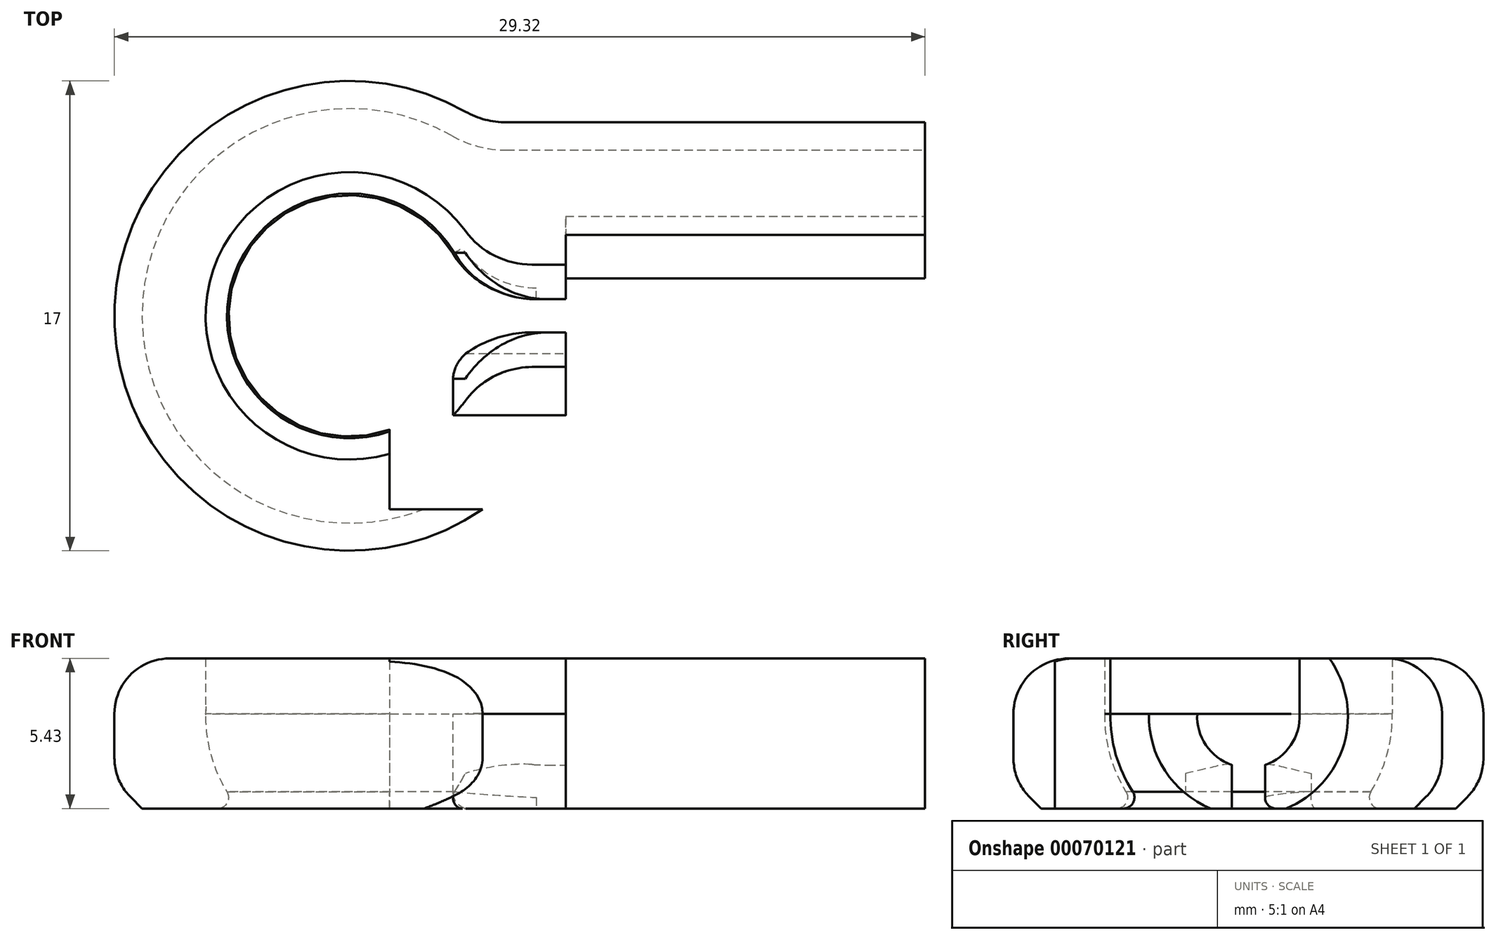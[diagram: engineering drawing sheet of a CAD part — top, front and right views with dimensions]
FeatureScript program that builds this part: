
annotation { "Feature Type Name" : "Feature", "Feature Type Description" : "" }
export const myFeature = defineFeature(function(context is Context, id is Id, definition is map)
    precondition{}
    {
        {
            assignVariable(context, id + "F0", {"name" : "ball", "anyValue" : 10});
        }
        {
            var Q0;
            Q0=qCreatedBy(makeId("Top.planeOp"),FACE);
            var sketch = newSketch(context, id + "F1", { "sketchPlane" : qUnion([Q0])});
            skCircle(sketch, "E0", {"center": v(0, 0) * mm, "radius": 5.2 * mm});
            skLineSegment(sketch, "E1", {"start": v(-13.72, 0) * mm, "end": v(11.71, 0) * mm});
            skCircle(sketch, "E2.0", {"center": v(0, 0) * mm, "radius": 8.5 * mm});
            skCircle(sketch, "E3", {"center": v(-8.1, 0) * mm, "radius": 2.9 * mm, "construction": true});
            skCircle(sketch, "E4", {"center": v(-8.1, 0) * mm, "radius": 1.4 * mm, "construction": true});
            skLineSegment(sketch, "E5.rect.bottom", {"start": v(4.82, 7) * mm, "end": v(20.82, 7) * mm});
            skLineSegment(sketch, "E5.rect.top", {"start": v(4.82, -7) * mm, "end": v(20.82, -7) * mm});
            skLineSegment(sketch, "E5.rect.left", {"start": v(4.82, 7) * mm, "end": v(4.82, -7) * mm, "construction": true});
            skLineSegment(sketch, "E5.rect.right", {"start": v(20.82, 7) * mm, "end": v(20.82, -7) * mm});
            skPoint(sketch, "E5.rect.middle", {"position": v(12.82, 0) * mm});
            skSolve(sketch);
        }
        {
            var Q0;
            {var subQ0=sQuery(id+"F1.wireOp",EDGE,"E1");var subQ1=sQuery(id+"F1.wireOp",EDGE,"E0");var subQ2=makeQuery(id+"F1.imprint","INTERSECT",VERTEX,{"disambiguationData":[OD(0.0)],"derivedFrom":[subQ1,subQ0]});Q0=makeQuery(id+"F1.imprint","IMPRINT",FACE,{"disambiguationData":[TD([[makeQuery(id+"F1.imprint","IMPRINT",EDGE,{"disambiguationData":[TD([[subQ2,-1.0]])],"derivedFrom":subQ1}),-1.0]])]});}
            var Q1;
            {var subQ0=sQuery(id+"F1.wireOp",EDGE,"E1");var subQ1=sQuery(id+"F1.wireOp",EDGE,"E0");var subQ2=makeQuery(id+"F1.imprint","INTERSECT",VERTEX,{"disambiguationData":[OD(0.0)],"derivedFrom":[subQ1,subQ0]});Q1=makeQuery(id+"F1.imprint","IMPRINT",FACE,{"disambiguationData":[TD([[makeQuery(id+"F1.imprint","IMPRINT",EDGE,{"disambiguationData":[TD([[subQ2,1.0]])],"derivedFrom":subQ1}),-1.0]])]});}
            var Q2;
            {var subQ4=sQuery(id+"F1.wireOp",EDGE,"E5.rect.bottom");Q2=makeQuery(id+"F1.imprint","IMPRINT",FACE,{"disambiguationData":[TD([[makeQuery(id+"F1.imprint","IMPRINT",EDGE,{"derivedFrom":subQ4}),-1.0]])]});}
            var Q3;
            {var subQ0=sQuery(id+"F1.wireOp",EDGE,"E2.0");var subQ1=sQuery(id+"F1.wireOp",EDGE,"E1");var subQ2=makeQuery(id+"F1.imprint","INTERSECT",VERTEX,{"disambiguationData":[OD(0.0)],"derivedFrom":[subQ1,subQ0]});Q3=makeQuery(id+"F1.imprint","IMPRINT",FACE,{"disambiguationData":[TD([[makeQuery(id+"F1.imprint","IMPRINT",EDGE,{"disambiguationData":[TD([[subQ2,1.0]])],"derivedFrom":subQ1}),1.0]])]});}
            var Q4;
            {var subQ0=sQuery(id+"F1.wireOp",EDGE,"E2.0");var subQ1=sQuery(id+"F1.wireOp",EDGE,"E1");var subQ2=makeQuery(id+"F1.imprint","INTERSECT",VERTEX,{"disambiguationData":[OD(0.0)],"derivedFrom":[subQ1,subQ0]});Q4=makeQuery(id+"F1.imprint","IMPRINT",FACE,{"disambiguationData":[TD([[makeQuery(id+"F1.imprint","IMPRINT",EDGE,{"disambiguationData":[TD([[subQ2,1.0]])],"derivedFrom":subQ1}),-1.0]])]});}
            var Q5;
            {var subQ0=sQuery(id+"F1.wireOp",EDGE,"E4");var subQ1=sQuery(id+"F1.wireOp",EDGE,"E1");var subQ2=makeQuery(id+"F1.imprint","INTERSECT",VERTEX,{"disambiguationData":[OD(1.0)],"derivedFrom":[subQ1,subQ0]});Q5=makeQuery(id+"F1.imprint","IMPRINT",FACE,{"disambiguationData":[TD([[makeQuery(id+"F1.imprint","IMPRINT",EDGE,{"disambiguationData":[TD([[subQ2,-1.0]])],"derivedFrom":subQ1}),1.0]])]});}
            var Q6;
            {var subQ0=sQuery(id+"F1.wireOp",EDGE,"E4");var subQ1=sQuery(id+"F1.wireOp",EDGE,"E1");var subQ2=makeQuery(id+"F1.imprint","INTERSECT",VERTEX,{"disambiguationData":[OD(1.0)],"derivedFrom":[subQ1,subQ0]});Q6=makeQuery(id+"F1.imprint","IMPRINT",FACE,{"disambiguationData":[TD([[makeQuery(id+"F1.imprint","IMPRINT",EDGE,{"disambiguationData":[TD([[subQ2,-1.0]])],"derivedFrom":subQ1}),-1.0]])]});}
            var Q7;
            {var subQ0=sQuery(id+"F1.wireOp",EDGE,"E1");var subQ1=sQuery(id+"F1.wireOp",EDGE,"E0");var subQ2=makeQuery(id+"F1.imprint","INTERSECT",VERTEX,{"disambiguationData":[OD(0.0)],"derivedFrom":[subQ1,subQ0]});Q7=makeQuery(id+"F1.imprint","IMPRINT",FACE,{"disambiguationData":[TD([[makeQuery(id+"F1.imprint","IMPRINT",EDGE,{"disambiguationData":[TD([[subQ2,1.0]])],"derivedFrom":subQ1}),1.0]])]});}
            var Q8;
            {var subQ0=sQuery(id+"F1.wireOp",EDGE,"E1");var subQ1=sQuery(id+"F1.wireOp",EDGE,"E0");var subQ2=makeQuery(id+"F1.imprint","INTERSECT",VERTEX,{"disambiguationData":[OD(0.0)],"derivedFrom":[subQ1,subQ0]});Q8=makeQuery(id+"F1.imprint","IMPRINT",FACE,{"disambiguationData":[TD([[makeQuery(id+"F1.imprint","IMPRINT",EDGE,{"disambiguationData":[TD([[subQ2,-1.0]])],"derivedFrom":subQ1}),1.0]])]});}
            extrude(context, id + "F2", {"entities" : qUnion([Q0, Q1, Q2, Q3, Q4, Q5, Q6, Q7, Q8]), "depth" : 0.1 * mm, "hasSecondDirection" : true, "secondDirectionOppositeDirection" : true, "secondDirectionDepth" : (getVariable(context, 'ball') / 3) * mm});
        }
        {
            var Q0;
            {var subQ0=sQuery(id+"F1.wireOp",EDGE,"E1");var subQ1=sQuery(id+"F1.wireOp",EDGE,"E0");var subQ2=makeQuery(id+"F1.imprint","INTERSECT",VERTEX,{"disambiguationData":[OD(0.0)],"derivedFrom":[subQ1,subQ0]});Q0=makeQuery(id+"F1.imprint","IMPRINT",FACE,{"disambiguationData":[TD([[makeQuery(id+"F1.imprint","IMPRINT",EDGE,{"disambiguationData":[TD([[subQ2,-1.0]])],"derivedFrom":subQ1}),1.0]])]});}
            var Q1;
            Q1=sQuery(id+"F1.wireOp",EDGE,"E1");
            revolve(context, id + "F3", {"operationType" : NewBodyOperationType.REMOVE, "entities" : qUnion([Q0]), "axis" : qUnion([Q1]), "revolveType" : RevolveType.FULL, "oppositeDirection" : true});
        }
        {
            var Q0;
            Q0=makeQuery(id+"F2.opExtrude","SWEPT_FACE",FACE,{"disambiguationData":[OSD([sQuery(id+"F1.wireOp",EDGE,"E5.rect.right")])]});
            var sketch = newSketch(context, id + "F4", { "sketchPlane" : qUnion([Q0])});
            skArc(sketch, "E6", {"start": v(-1.85, 3.09) * mm, "mid": v(0, -3.6) * mm, "end": v(1.85, 3.09) * mm});
            skArc(sketch, "E7", {"start": v(-1.85, 0.1) * mm, "mid": v(0, -1.85) * mm, "end": v(1.85, 0.1) * mm});
            skLineSegment(sketch, "E8.bottom", {"start": v(1.85, 0.1) * mm, "end": v(-1.85, 0.1) * mm});
            skLineSegment(sketch, "E8.top", {"start": v(1.85, 5.18) * mm, "end": v(-1.85, 5.18) * mm});
            skLineSegment(sketch, "E8.left", {"start": v(1.85, 0.1) * mm, "end": v(1.85, 5.18) * mm});
            skLineSegment(sketch, "E8.right", {"start": v(-1.85, 0.1) * mm, "end": v(-1.85, 5.18) * mm});
            skPoint(sketch, "E8.middle", {"position": v(0, 2.64) * mm});
            skSolve(sketch);
        }
        {
            var Q0;
            Q0=makeQuery(id+"F2.opExtrude","CAP_FACE",FACE,{"disambiguationData":[OSD([sQuery(id+"F1.wireOp",EDGE,"E2.0"),sQuery(id+"F1.wireOp",EDGE,"E4"),sQuery(id+"F1.wireOp",EDGE,"E5.rect.bottom"),sQuery(id+"F1.wireOp",EDGE,"E5.rect.top"),sQuery(id+"F1.wireOp",EDGE,"E5.rect.right")])],"isStart":false});
            var sketch = newSketch(context, id + "F5", { "sketchPlane" : qUnion([Q0])});
            skPoint(sketch, "E9.0", {"position": v(0, 0) * mm});
            skCircle(sketch, "E10", {"center": v(0, 0) * mm, "radius": 5.8 * mm, "construction": true});
            skCircle(sketch, "E11.0", {"center": v(0, 0) * mm, "radius": 6 * mm, "construction": true});
            skLineSegment(sketch, "E12.rect.bottom", {"start": v(-5.78, 0.5) * mm, "end": v(0.17, 0.5) * mm, "construction": true});
            skLineSegment(sketch, "E12.rect.top", {"start": v(-5.78, -0.5) * mm, "end": v(0.17, -0.5) * mm, "construction": true});
            skLineSegment(sketch, "E12.rect.left", {"start": v(-5.78, 0.5) * mm, "end": v(-5.78, -0.5) * mm, "construction": true});
            skLineSegment(sketch, "E12.rect.right", {"start": v(0.17, 0.5) * mm, "end": v(0.17, -0.5) * mm, "construction": true});
            skPoint(sketch, "E12.rect.middle", {"position": v(-2.8, 0) * mm});
            skLineSegment(sketch, "E13.bottom", {"start": v(19.5, 0.6) * mm, "end": v(-3.53, 0.6) * mm});
            skLineSegment(sketch, "E13.top", {"start": v(19.5, -0.6) * mm, "end": v(-3.53, -0.6) * mm});
            skLineSegment(sketch, "E13.left", {"start": v(19.5, 0.6) * mm, "end": v(19.5, -0.6) * mm});
            skLineSegment(sketch, "E13.right", {"start": v(-3.53, 0.6) * mm, "end": v(-3.53, -0.6) * mm});
            skPoint(sketch, "E13.middle", {"position": v(7.98, 0) * mm});
            skSolve(sketch);
        }
        {
            var Q0;
            Q0=makeQuery(id+"F2.opExtrude","CAP_FACE",FACE,{"disambiguationData":[OSD([sQuery(id+"F1.wireOp",EDGE,"E2.0"),sQuery(id+"F1.wireOp",EDGE,"E5.rect.bottom"),sQuery(id+"F1.wireOp",EDGE,"E5.rect.top"),sQuery(id+"F1.wireOp",EDGE,"E5.rect.right")])],"isStart":false});
            extrude(context, id + "F6", {"entities" : qUnion([Q0]), "operationType" : NewBodyOperationType.ADD, "depth" : 2 * mm});
        }
        {
            var Q0;
            {var subQ0=sQuery(id+"F5.wireOp",EDGE,"E13.left");Q0=makeQuery(id+"F5.imprint","IMPRINT",FACE,{"disambiguationData":[TD([[makeQuery(id+"F5.imprint","IMPRINT",EDGE,{"derivedFrom":subQ0}),-1.0]])]});}
            var Q1;
            {var subQ0=sQuery(id+"F5.wireOp",EDGE,"E13.right");Q1=makeQuery(id+"F5.imprint","IMPRINT",FACE,{"disambiguationData":[TD([[makeQuery(id+"F5.imprint","IMPRINT",EDGE,{"derivedFrom":subQ0}),1.0]])]});}
            extrude(context, id + "F7", {"entities" : qUnion([Q0, Q1]), "operationType" : NewBodyOperationType.REMOVE, "endBound" : BoundingType.SYMMETRIC, "oppositeDirection" : true, "depth" : 25 * mm});
        }
        {
            var Q0;
            Q0=makeQuery(id+"F4.imprint","IMPRINT",FACE,{"disambiguationData":[TD([[makeQuery(id+"F4.imprint","IMPRINT",EDGE,{"derivedFrom":sQuery(id+"F4.wireOp",EDGE,"E6")}),1.0]])]});
            var Q1;
            {var subQ0=sQuery(id+"F4.wireOp",EDGE,"E6");var subQ1=makeQuery(id+"F2.opExtrude","CAP_EDGE",EDGE,{"disambiguationData":[OSD([sQuery(id+"F1.wireOp",EDGE,"E5.rect.right")])],"isStart":false});var subQ2=makeQuery(id+"F4.imprint","INTERSECT",VERTEX,{"disambiguationData":[OD(0.0)],"derivedFrom":[subQ1,subQ0]});Q1=makeQuery(id+"F4.imprint","IMPRINT",FACE,{"disambiguationData":[TD([[makeQuery(id+"F4.imprint","IMPRINT",EDGE,{"disambiguationData":[TD([[subQ2,1.0]])],"derivedFrom":subQ0}),1.0]])]});}
            var Q2;
            {var subQ0=sQuery(id+"F4.wireOp",EDGE,"E8.left");var subQ1=sQuery(id+"F4.wireOp",EDGE,"E6");var subQ2=makeQuery(id+"F4.imprint","INTERSECT",VERTEX,{"derivedFrom":[subQ1,subQ0]});Q2=makeQuery(id+"F4.imprint","IMPRINT",FACE,{"disambiguationData":[TD([[makeQuery(id+"F4.imprint","IMPRINT",EDGE,{"disambiguationData":[TD([[subQ2,1.0]])],"derivedFrom":subQ1}),1.0]])]});}
            extrude(context, id + "F8", {"entities" : qUnion([Q0, Q1, Q2]), "operationType" : NewBodyOperationType.REMOVE, "oppositeDirection" : true, "depth" : 13 * mm});
        }
        {
            var Q0;
            {var subQ0=sQuery(id+"F1.wireOp",EDGE,"E5.rect.right");Q0=makeQuery(id+"F8.boolean.opBoolean","SPLIT",FACE,{"disambiguationData":[TD([makeQuery(id+"F8.opExtrude","SWEPT_FACE",FACE,{"disambiguationData":[OSD([sQuery(id+"F4.wireOp",EDGE,"E7")])]})])],"derivedFrom":makeQuery(id+"F2.opExtrude","SWEPT_FACE",FACE,{"disambiguationData":[OSD([subQ0])]})});}
            extrude(context, id + "F9", {"entities" : qUnion([Q0]), "operationType" : NewBodyOperationType.REMOVE, "oppositeDirection" : true, "depth" : 19.37 * mm});
        }
        {
            var Q0;
            Q0=makeQuery(id+"F2.opExtrude","SWEPT_EDGE",EDGE,{"disambiguationData":[OSD([sQuery(id+"F1.wireOp",EDGE,"E2.0"),sQuery(id+"F1.wireOp",EDGE,"E5.rect.top")])]});
            var Q1;
            Q1=makeQuery(id+"F2.opExtrude","SWEPT_EDGE",EDGE,{"disambiguationData":[OSD([sQuery(id+"F1.wireOp",EDGE,"E2.0"),sQuery(id+"F1.wireOp",EDGE,"E5.rect.bottom")])]});
            fillet(context, id + "F10", {"entities" : qUnion([Q0, Q1]), "radius" : 3 * mm, "tangentPropagation" : true, "allowEdgeOverflow" : false});
        }
        {
            var Q0;
            Q0=makeQuery(id+"F2.opExtrude","CAP_EDGE",EDGE,{"disambiguationData":[OSD([sQuery(id+"F1.wireOp",EDGE,"E2.0")])],"isStart":true});
            chamfer(context, id + "F11", {"entities" : qUnion([Q0]), "width" : 1 * mm, "tangentPropagation" : true});
        }
        {
            var Q0;
            {var subQ0=sQuery(id+"F1.wireOp",EDGE,"E2.0");Q0=makeQuery(id+"F11.opChamfer","BLEND_EDGE",EDGE,{"blendedFrom":[makeQuery(id+"F2.opExtrude","CAP_EDGE",EDGE,{"disambiguationData":[OSD([subQ0])],"isStart":false}),makeQuery(id+"F2.opExtrude","SWEPT_FACE",FACE,{"disambiguationData":[OSD([subQ0])]})],"blendedInto":[makeQuery(id+"F2.opExtrude","SWEPT_FACE",FACE,{"disambiguationData":[OSD([subQ0])]})]});}
            var Q1;
            {var subQ0=sQuery(id+"F1.wireOp",EDGE,"E2.0");Q1=makeQuery(id+"F11.opChamfer","BLEND_EDGE",EDGE,{"blendedFrom":[makeQuery(id+"F2.opExtrude","CAP_EDGE",EDGE,{"disambiguationData":[OSD([subQ0])],"isStart":true}),makeQuery(id+"F2.opExtrude","SWEPT_FACE",FACE,{"disambiguationData":[OSD([subQ0])]})],"blendedInto":[makeQuery(id+"F2.opExtrude","SWEPT_FACE",FACE,{"disambiguationData":[OSD([subQ0])]})]});}
            var Q2;
            Q2=makeQuery(id+"F6.opExtrude","CAP_EDGE",EDGE,{"disambiguationData":[OSD([sQuery(id+"F1.wireOp",EDGE,"E2.0")])],"isStart":false});
            fillet(context, id + "F12", {"entities" : qUnion([Q0, Q1, Q2]), "radius" : 2 * mm, "tangentPropagation" : true, "allowEdgeOverflow" : false});
        }
        {
            var Q0;
            Q0=makeQuery(id+"F9.boolean.opBoolean","INTERSECT",EDGE,{"derivedFrom":[makeQuery(id+"F3.boolean.opBoolean","COPY",FACE,{"derivedFrom":makeQuery(id+"F3.opRevolve","SWEPT_FACE",FACE,{"disambiguationData":[OSD([sQuery(id+"F1.wireOp",EDGE,"E0")])]})}),makeQuery(id+"F9.opExtrude","SWEPT_FACE",FACE,{"disambiguationData":[OSD([sQuery(id+"F4.wireOp",EDGE,"E7")])]})]});
            var Q1;
            Q1=makeQuery(id+"F9.boolean.opBoolean","INTERSECT",EDGE,{"derivedFrom":[makeQuery(id+"F6.opExtrude","SWEPT_FACE",FACE,{"disambiguationData":[OSD([sQuery(id+"F1.wireOp",EDGE,"E0"),sQuery(id+"F1.wireOp",EDGE,"E2.0"),sQuery(id+"F1.wireOp",EDGE,"E5.rect.bottom"),sQuery(id+"F1.wireOp",EDGE,"E5.rect.top"),sQuery(id+"F1.wireOp",EDGE,"E5.rect.right")])]}),makeQuery(id+"F9.opExtrude","SWEPT_FACE",FACE,{"disambiguationData":[OSD([sQuery(id+"F4.wireOp",EDGE,"E8.right")])]})]});
            var Q2;
            Q2=makeQuery(id+"F9.boolean.opBoolean","INTERSECT",EDGE,{"derivedFrom":[makeQuery(id+"F6.opExtrude","SWEPT_FACE",FACE,{"disambiguationData":[OSD([sQuery(id+"F1.wireOp",EDGE,"E0"),sQuery(id+"F1.wireOp",EDGE,"E2.0"),sQuery(id+"F1.wireOp",EDGE,"E5.rect.bottom"),sQuery(id+"F1.wireOp",EDGE,"E5.rect.top"),sQuery(id+"F1.wireOp",EDGE,"E5.rect.right")])]}),makeQuery(id+"F9.opExtrude","SWEPT_FACE",FACE,{"disambiguationData":[OSD([sQuery(id+"F4.wireOp",EDGE,"E8.left")])]})]});
            var Q3;
            Q3=makeQuery(id+"F7.boolean.opBoolean","INTERSECT",EDGE,{"derivedFrom":[makeQuery(id+"F3.boolean.opBoolean","COPY",FACE,{"derivedFrom":makeQuery(id+"F3.opRevolve","SWEPT_FACE",FACE,{"disambiguationData":[OSD([sQuery(id+"F1.wireOp",EDGE,"E0")])]})}),makeQuery(id+"F7.opExtrude","SWEPT_FACE",FACE,{"disambiguationData":[OSD([sQuery(id+"F5.wireOp",EDGE,"E13.top")])]})]});
            var Q4;
            Q4=makeQuery(id+"F7.boolean.opBoolean","INTERSECT",EDGE,{"derivedFrom":[makeQuery(id+"F3.boolean.opBoolean","COPY",FACE,{"derivedFrom":makeQuery(id+"F3.opRevolve","SWEPT_FACE",FACE,{"disambiguationData":[OSD([sQuery(id+"F1.wireOp",EDGE,"E0")])]})}),makeQuery(id+"F7.opExtrude","SWEPT_FACE",FACE,{"disambiguationData":[OSD([sQuery(id+"F5.wireOp",EDGE,"E13.bottom")])]})]});
            fillet(context, id + "F13", {"entities" : qUnion([Q0, Q1, Q2, Q3, Q4]), "radius" : 3 * mm, "tangentPropagation" : true, "allowEdgeOverflow" : false});
        }
        {
            var Q0;
            Q0=makeQuery(id+"F3.boolean.opBoolean","INTERSECT",EDGE,{"derivedFrom":[makeQuery(id+"F2.opExtrude","CAP_FACE",FACE,{"disambiguationData":[OSD([sQuery(id+"F1.wireOp",EDGE,"E2.0"),sQuery(id+"F1.wireOp",EDGE,"E5.rect.bottom"),sQuery(id+"F1.wireOp",EDGE,"E5.rect.top"),sQuery(id+"F1.wireOp",EDGE,"E5.rect.right")])],"isStart":false}),makeQuery(id+"F3.opRevolve","SWEPT_FACE",FACE,{"disambiguationData":[OSD([sQuery(id+"F1.wireOp",EDGE,"E0")])]})]});
            var Q1;
            Q1=makeQuery(id+"F13.opFillet","BLEND_EDGE",EDGE,{"blendedFrom":[makeQuery(id+"F8.boolean.opBoolean","INTERSECT",EDGE,{"disambiguationData":[OD(1.0)],"derivedFrom":[makeQuery(id+"F3.boolean.opBoolean","COPY",FACE,{"derivedFrom":makeQuery(id+"F3.opRevolve","SWEPT_FACE",FACE,{"disambiguationData":[OSD([sQuery(id+"F1.wireOp",EDGE,"E0")])]})}),makeQuery(id+"F8.opExtrude","SWEPT_FACE",FACE,{"disambiguationData":[OSD([sQuery(id+"F4.wireOp",EDGE,"E6")])]})]}),makeQuery(id+"F2.opExtrude","CAP_FACE",FACE,{"disambiguationData":[OSD([sQuery(id+"F1.wireOp",EDGE,"E2.0"),sQuery(id+"F1.wireOp",EDGE,"E5.rect.bottom"),sQuery(id+"F1.wireOp",EDGE,"E5.rect.top"),sQuery(id+"F1.wireOp",EDGE,"E5.rect.right")])],"isStart":false})],"blendedInto":[makeQuery(id+"F2.opExtrude","CAP_FACE",FACE,{"disambiguationData":[OSD([sQuery(id+"F1.wireOp",EDGE,"E2.0"),sQuery(id+"F1.wireOp",EDGE,"E5.rect.bottom"),sQuery(id+"F1.wireOp",EDGE,"E5.rect.top"),sQuery(id+"F1.wireOp",EDGE,"E5.rect.right")])],"isStart":false})]});
            var Q2;
            Q2=makeQuery(id+"F13.opFillet","BLEND_EDGE",EDGE,{"blendedFrom":[makeQuery(id+"F8.boolean.opBoolean","INTERSECT",EDGE,{"disambiguationData":[OD(0.0)],"derivedFrom":[makeQuery(id+"F3.boolean.opBoolean","COPY",FACE,{"derivedFrom":makeQuery(id+"F3.opRevolve","SWEPT_FACE",FACE,{"disambiguationData":[OSD([sQuery(id+"F1.wireOp",EDGE,"E0")])]})}),makeQuery(id+"F8.opExtrude","SWEPT_FACE",FACE,{"disambiguationData":[OSD([sQuery(id+"F4.wireOp",EDGE,"E6")])]})]}),makeQuery(id+"F2.opExtrude","CAP_FACE",FACE,{"disambiguationData":[OSD([sQuery(id+"F1.wireOp",EDGE,"E2.0"),sQuery(id+"F1.wireOp",EDGE,"E5.rect.bottom"),sQuery(id+"F1.wireOp",EDGE,"E5.rect.top"),sQuery(id+"F1.wireOp",EDGE,"E5.rect.right")])],"isStart":false})],"blendedInto":[makeQuery(id+"F2.opExtrude","CAP_FACE",FACE,{"disambiguationData":[OSD([sQuery(id+"F1.wireOp",EDGE,"E2.0"),sQuery(id+"F1.wireOp",EDGE,"E5.rect.bottom"),sQuery(id+"F1.wireOp",EDGE,"E5.rect.top"),sQuery(id+"F1.wireOp",EDGE,"E5.rect.right")])],"isStart":false})]});
            var Q3;
            Q3=makeQuery(id+"F7.boolean.opBoolean","COPY",EDGE,{"derivedFrom":makeQuery(id+"F7.opExtrude","CAP_EDGE",EDGE,{"disambiguationData":[OSD([sQuery(id+"F5.wireOp",EDGE,"E13.bottom")])],"isStart":true})});
            var Q4;
            Q4=makeQuery(id+"F7.boolean.opBoolean","COPY",EDGE,{"derivedFrom":makeQuery(id+"F7.opExtrude","CAP_EDGE",EDGE,{"disambiguationData":[OSD([sQuery(id+"F5.wireOp",EDGE,"E13.top")])],"isStart":true})});
            var Q5;
            Q5=makeQuery(id+"F3.boolean.opBoolean","INTERSECT",EDGE,{"derivedFrom":[makeQuery(id+"F2.opExtrude","CAP_FACE",FACE,{"disambiguationData":[OSD([sQuery(id+"F1.wireOp",EDGE,"E2.0"),sQuery(id+"F1.wireOp",EDGE,"E5.rect.bottom"),sQuery(id+"F1.wireOp",EDGE,"E5.rect.top"),sQuery(id+"F1.wireOp",EDGE,"E5.rect.right")])],"isStart":true}),makeQuery(id+"F3.opRevolve","SWEPT_FACE",FACE,{"disambiguationData":[OSD([sQuery(id+"F1.wireOp",EDGE,"E0")])]})]});
            fillet(context, id + "F14", {"entities" : qUnion([Q0, Q1, Q2, Q3, Q4, Q5]), "radius" : 0.4 * mm, "tangentPropagation" : true, "allowEdgeOverflow" : false});
        }
    });
